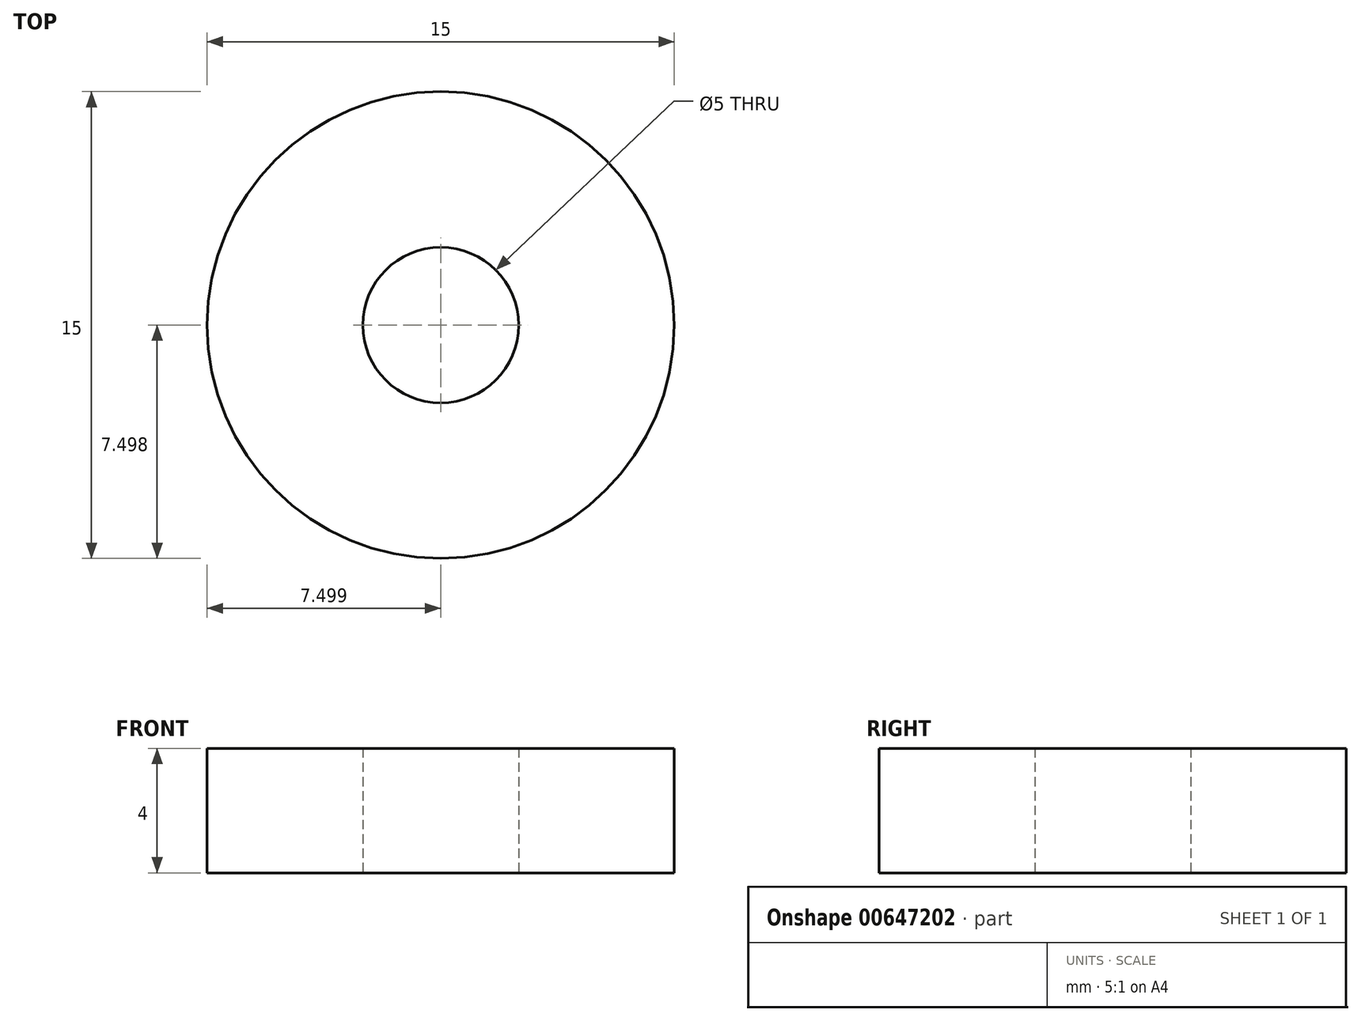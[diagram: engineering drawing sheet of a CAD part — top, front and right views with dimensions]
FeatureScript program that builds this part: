
annotation { "Feature Type Name" : "Feature", "Feature Type Description" : "" }
export const myFeature = defineFeature(function(context is Context, id is Id, definition is map)
    precondition{}
    {
        {
            var Q0;
            Q0=qCreatedBy(makeId("Top.planeOp"),FACE);
            var sketch = newSketch(context, id + "F0", { "sketchPlane" : qUnion([Q0])});
            skCircle(sketch, "E0", {"center": v(-31.18, 40.25) * mm, "radius": 2.5 * mm});
            skCircle(sketch, "E1.0", {"center": v(-31.18, 40.25) * mm, "radius": 7.5 * mm});
            skSolve(sketch);
        }
        {
            var Q0;
            Q0=makeQuery(id+"F0.imprint","IMPRINT",FACE,{"disambiguationData":[TD([[makeQuery(id+"F0.imprint","IMPRINT",EDGE,{"derivedFrom":sQuery(id+"F0.wireOp",EDGE,"E0")}),-1.0]])]});
            extrude(context, id + "F1", {"entities" : qUnion([Q0]), "depth" : 4 * mm, "offsetDistance" : 25 * mm});
        }
    });
